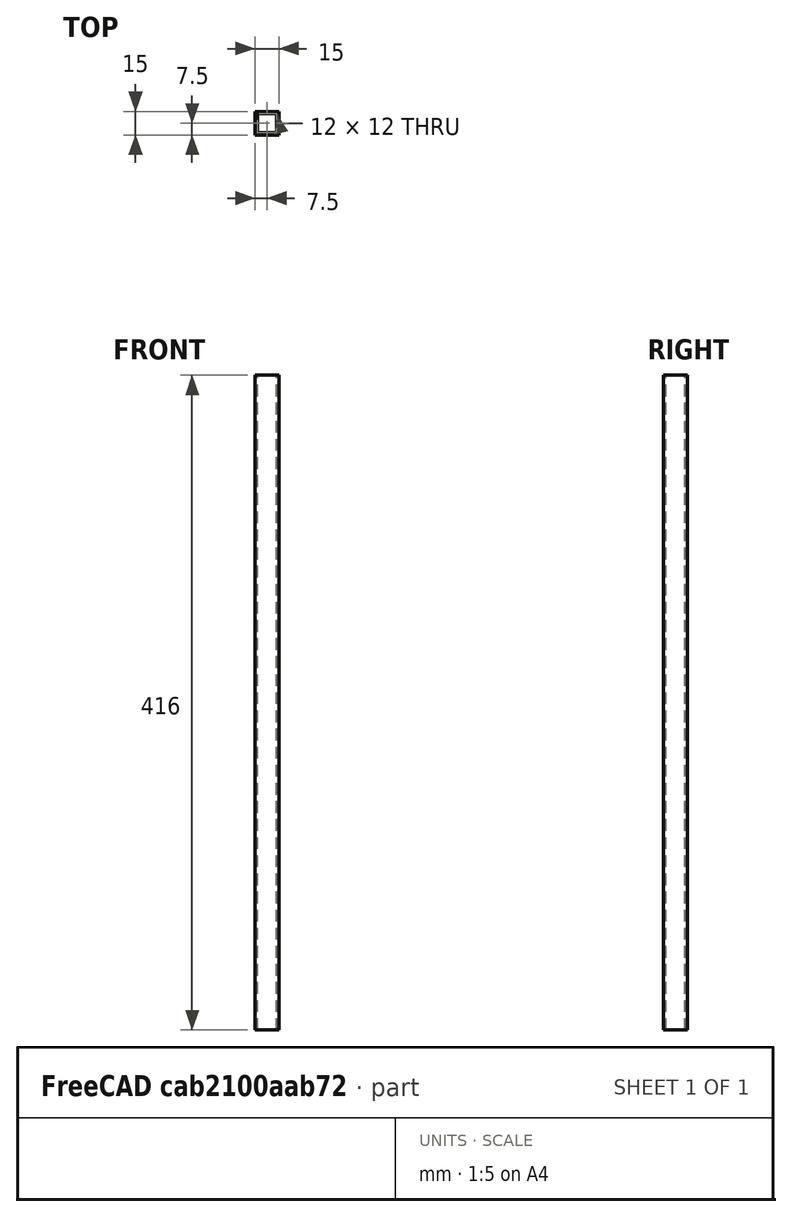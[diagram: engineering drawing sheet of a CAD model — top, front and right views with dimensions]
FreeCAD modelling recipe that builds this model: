
FCSTD DOCUMENT  (FreeCAD 0.16R6698 (Git))
Label: Tube 552
License: All rights reserved
LicenseURL: http://en.wikipedia.org/wiki/All_rights_reserved
objects: Sketcher::SketchObject×1, PartDesign::Pad×1
note: 3 computed .brp shape members not serialized (recipe doc carries the construction recipe); baked Part::Feature solids carry a one-line shape summary decoded from their .brp

FEATURE [Sketcher::SketchObject] Sketch
  sketch-geometry (8):
    g0: LineSegment StartX=-7.5 StartY=7.5 StartZ=0 EndX=7.5 EndY=7.5 EndZ=0
    g1: LineSegment StartX=7.5 StartY=7.5 StartZ=0 EndX=7.5 EndY=-7.5 EndZ=0
    g2: LineSegment StartX=7.5 StartY=-7.5 StartZ=0 EndX=-7.5 EndY=-7.5 EndZ=0
    g3: LineSegment StartX=-7.5 StartY=-7.5 StartZ=0 EndX=-7.5 EndY=7.5 EndZ=0
    g4: LineSegment StartX=-6 StartY=6 StartZ=0 EndX=6 EndY=6 EndZ=0
    g5: LineSegment StartX=6 StartY=6 StartZ=0 EndX=6 EndY=-6 EndZ=0
    g6: LineSegment StartX=6 StartY=-6 StartZ=0 EndX=-6 EndY=-6 EndZ=0
    g7: LineSegment StartX=-6 StartY=-6 StartZ=0 EndX=-6 EndY=6 EndZ=0
  constraints (24):
    c: Coincident(g0,g1)
    c: Coincident(g1,g2)
    c: Coincident(g2,g3)
    c: Coincident(g3,g0)
    c: Horizontal(g0)
    c: Horizontal(g2)
    c: Vertical(g1)
    c: Vertical(g3)
    c: Coincident(g4,g5)
    c: Coincident(g5,g6)
    c: Coincident(g6,g7)
    c: Coincident(g7,g4)
    c: Horizontal(g4)
    c: Horizontal(g6)
    c: Vertical(g5)
    c: Vertical(g7)
    c: DistanceX(g0,g0) = 15
    c: DistanceY(g1,g1) = 15
    c: DistanceX(g0,g4) = 1.5
    c: DistanceX(g4,g0) = 1.5
    c: DistanceY(g4,g0) = 1.5
    c: DistanceY(g1,g5) = 1.5
    c: DistanceX(g0,g-1) = 7.5
    c: DistanceY(g1,g-1) = 7.5
FEATURE [PartDesign::Pad] Pad
  Length = 416
  Length2 = 100
  Sketch = -> Sketch
  Type = 0
